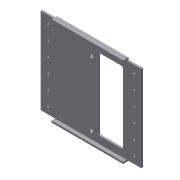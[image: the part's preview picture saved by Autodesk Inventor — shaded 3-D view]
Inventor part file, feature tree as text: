
AUTODESK INVENTOR PART (.ipt)
format: ipt  version: 2012 (Build 160160000, 160)  size: 155,648 bytes
history: native  units: in
note: dims shown in document units (in); Inventor stores cm internally (conversion verified against a paired STEP export)
features: extrude x5, sketch x5
ambient origin geometry x8: Origin, YZ Plane, XZ Plane, XY Plane, X Axis, Y Axis, Z Axis, Center Point
feature tree (10):
  extrude  "Extrusion3"  Depth=7.0in
  extrude  "Extrusion4"  Depth=1.0in
  extrude  "Extrusion5"  Depth=0.125in TaperAngle=0.0deg
  extrude  "Extrusion6"  Depth=1.0in
  extrude  "Extrusion7"  Depth=0.5in
  sketch  "Sketch1"  dims[d0=6.0in d1=7.0in]
  sketch  "Sketch2"  dims[d18=1.0in d19=1.0in]
  sketch  "Sketch3"  dims[d20=0.125in d24=0.125in d25=0.0in]
  sketch  "Sketch4"  dims[d26=0.5in d27=1.0in]
  sketch  "Sketch5"  dims[d28=0.1875in d29=0.5in d30=1.0in d31=0.1875in d32=0.125in d33=0.0in d34=3.5in d35=3.5in d36=4.5in d37=0.5in d38=0.25in d39=0.25in d40=0.125in d41=0.0in d42=0.5in d43=1.25in d44=0.5in d45=0.5in d46=0.125in d47=0.125in d48=0.0in d49=0.25in d50=0.0in]
